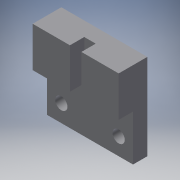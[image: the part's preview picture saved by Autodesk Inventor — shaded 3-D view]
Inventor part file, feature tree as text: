
AUTODESK INVENTOR PART (.ipt)
format: ipt  version: 2019 (Build 230136000, 136)  size: 118,784 bytes
history: native  units: in
note: dims shown in document units (in); Inventor stores cm internally (conversion verified against a paired STEP export)
features: extrude x2, sketch x2
ambient origin geometry x8: Origin, YZ Plane, XZ Plane, XY Plane, X Axis, Y Axis, Z Axis, Center Point
bodies: Solid1 (feature_tree)
feature tree (4):
  extrude  "Extrusion1"  Depth=1.1811in
  extrude  "Extrusion2"  Depth=0.1575in
  sketch  "Sketch1"  dims[d2=1.1811in d3=1.1811in]
  sketch  "Sketch2"  dims[d4=0.1969in d5=0.0in d6=0.1575in d7=0.5512in d8=0.3937in d9=0.0in d10=0.1673in d11=0.1673in d12=0.1969in d13=0.2362in]
